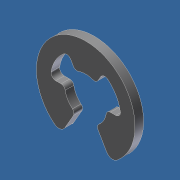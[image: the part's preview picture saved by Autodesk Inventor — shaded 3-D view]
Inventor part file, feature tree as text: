
AUTODESK INVENTOR PART (.ipt)
format: ipt  version: unknown  size: 201,728 bytes
history: native  units: in
note: dims shown in document units (in); Inventor stores cm internally (conversion verified against a paired STEP export)
features: other x7, extrude x1, sketch x1
ambient origin geometry x8: Origin, YZ Plane, XZ Plane, XY Plane, X Axis, Y Axis, Z Axis, Center Point
feature tree (9):
  extrude  "Extrusion1"  [1 undecoded]
  other  "RR_XY"
  other  "RR_YZ"
  other  "RR_ZX"
  other  "RR_X"
  other  "RR_Y"
  other  "RR_Z"
  other  "RR_Center"
  sketch  "Sketch_1"  dims[d0=0.0435in d1=0.0in]
note: 1 required parameter value undecoded (feature->parameter linkage not recoverable at this tier; creation-order binding heuristic only, values carry confidence <= 0.55)
